FCSTD DOCUMENT  (FreeCAD 0.21R33694 (Git))
Label: flexible solar backing
License: All rights reserved
LicenseURL: http://en.wikipedia.org/wiki/All_rights_reserved
objects: Sketcher::SketchObject×1, PartDesign::Pad×1, PartDesign::Body×1
note: 4 computed .brp shape members not serialized (recipe doc carries the construction recipe); baked Part::Feature solids carry a one-line shape summary decoded from their .brp

FEATURE [Sketcher::SketchObject] Sketch
  FullyConstrained = false
  MapMode = 5
  Support = -> [XY_Plane]
  sketch-geometry (16):
    g0: LineSegment StartX=-291 StartY=-546.5 StartZ=0 EndX=-291 EndY=546.5 EndZ=0
    g1: LineSegment StartX=-291 StartY=546.5 StartZ=0 EndX=291 EndY=546.5 EndZ=0
    g2: LineSegment StartX=291 StartY=546.5 StartZ=0 EndX=291 EndY=-546.5 EndZ=0
    g3: LineSegment StartX=291 StartY=-546.5 StartZ=0 EndX=-291 EndY=-546.5 EndZ=0
    g4: GeomPoint X=0 Y=0 Z=0
    g5: LineSegment StartX=-276 StartY=-531.5 StartZ=0 EndX=-276 EndY=531.5 EndZ=0
    g6: LineSegment StartX=-276 StartY=531.5 StartZ=0 EndX=276 EndY=531.5 EndZ=0
    g7: LineSegment StartX=276 StartY=531.5 StartZ=0 EndX=276 EndY=-531.5 EndZ=0
    g8: LineSegment StartX=276 StartY=-531.5 StartZ=0 EndX=-276 EndY=-531.5 EndZ=0
    g9: GeomPoint X=0 Y=0 Z=0
    g10: Circle CenterX=-275.797 CenterY=-531.5 CenterZ=0 NormalX=0 NormalY=0 NormalZ=1 AngleXU=0 Radius=3.125
    g11: Circle CenterX=276 CenterY=-531.5 CenterZ=0 NormalX=0 NormalY=0 NormalZ=1 AngleXU=0 Radius=3.125
    g12: Circle CenterX=276 CenterY=0 CenterZ=0 NormalX=0 NormalY=0 NormalZ=1 AngleXU=0 Radius=3.125
    g13: Circle CenterX=276 CenterY=531.5 CenterZ=0 NormalX=0 NormalY=0 NormalZ=1 AngleXU=0 Radius=3.125
    g14: Circle CenterX=-276 CenterY=531.5 CenterZ=0 NormalX=0 NormalY=0 NormalZ=1 AngleXU=0 Radius=3.125
    g15: Circle CenterX=-276 CenterY=0 CenterZ=0 NormalX=0 NormalY=0 NormalZ=1 AngleXU=0 Radius=3.125
  constraints (36):
    c: Coincident(g0,g1)
    c: Coincident(g1,g2)
    c: Coincident(g2,g3)
    c: Coincident(g3,g0)
    c: Horizontal(g1)
    c: Horizontal(g3)
    c: Vertical(g0)
    c: Vertical(g2)
    c: Symmetric(g1,g0,g4)
    c: Coincident(g4,g-1)
    c: DistanceX(g1,g1) = 582
    c: DistanceY(g0,g0) = 1093
    c: Coincident(g5,g6)
    c: Coincident(g6,g7)
    c: Coincident(g7,g8)
    c: Coincident(g8,g5)
    c: Horizontal(g6)
    c: Horizontal(g8)
    c: Vertical(g5)
    c: Vertical(g7)
    c: Symmetric(g6,g5,g9)
    c: Coincident(g9,g4)
    c: DistanceX(g0,g5) = 15
    c: DistanceY(g0,g5) = 15
    c: PointOnObject(g10,g8)
    c: Diameter(g10) = 6.25
    c: Coincident(g11,g7)
    c: PointOnObject(g12,g7)
    c: Coincident(g13,g6)
    c: Coincident(g14,g5)
    c: PointOnObject(g15,g5)
    c: Equal(g10,g11)
    c: Equal(g10,g15)
    c: Equal(g10,g12)
    c: Equal(g10,g14)
    c: Equal(g10,g13)
FEATURE [PartDesign::Pad] Pad
  Direction = (0,0,1)
  Length = 9
  Length2 = 10
  Profile = -> Sketch
  ReferenceAxis = -> Sketch [N_Axis]
  Type = 0
FEATURE [PartDesign::Body] Body
  Group = -> [Sketch,Pad]
  Origin = -> Origin
